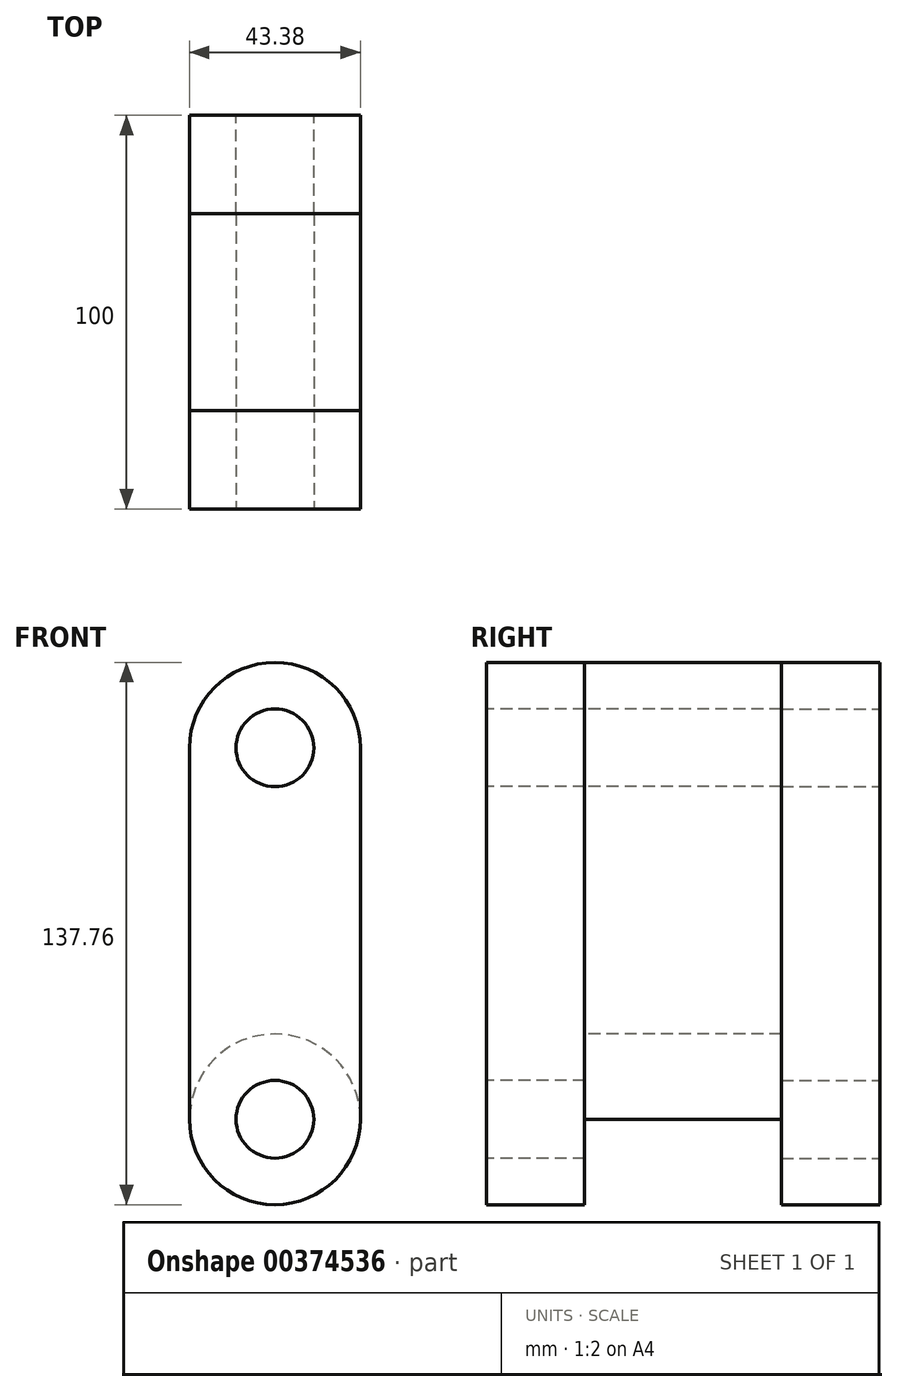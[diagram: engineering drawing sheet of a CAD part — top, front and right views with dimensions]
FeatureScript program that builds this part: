
annotation { "Feature Type Name" : "Feature", "Feature Type Description" : "" }
export const myFeature = defineFeature(function(context is Context, id is Id, definition is map)
    precondition{}
    {
        {
            var Q0;
            Q0=qCreatedBy(makeId("Front.planeOp"),FACE);
            var sketch = newSketch(context, id + "F0", { "sketchPlane" : qUnion([Q0])});
            skArc(sketch, "E0", {"start": v(-21.69, 0) * mm, "mid": v(0, -21.69) * mm, "end": v(21.69, 0) * mm});
            skArc(sketch, "E1", {"start": v(21.69, 94.38) * mm, "mid": v(0, 116.07) * mm, "end": v(-21.69, 94.38) * mm});
            skLineSegment(sketch, "E2", {"start": v(21.69, 94.38) * mm, "end": v(21.69, 0) * mm});
            skLineSegment(sketch, "E3", {"start": v(-21.69, 94.38) * mm, "end": v(-21.69, 0) * mm});
            skCircle(sketch, "E4", {"center": v(0, 94.38) * mm, "radius": 9.87 * mm});
            skCircle(sketch, "E5", {"center": v(0, 0) * mm, "radius": 9.87 * mm});
            skSolve(sketch);
        }
        {
            var Q0;
            Q0=makeQuery(id+"F0.imprint","IMPRINT",FACE,{"disambiguationData":[TD([[makeQuery(id+"F0.imprint","IMPRINT",EDGE,{"derivedFrom":sQuery(id+"F0.wireOp",EDGE,"E0")}),1.0]])]});
            extrude(context, id + "F1", {"entities" : qUnion([Q0]), "depth" : 25 * mm});
        }
        {
            var Q0;
            Q0=qCreatedBy(makeId("Front.planeOp"),FACE);
            cPlane(context, id + "F2", {"entities" : qUnion([Q0]), "cplaneType" : CPlaneType.OFFSET, "offset" : 50 * mm, "width" : 150 * mm, "height" : 150 * mm});
        }
        {
            var Q0;
            Q0=makeQuery(id+"F1.opExtrude","SWEPT_BODY",BODY,{"disambiguationData":[OSD([sQuery(id+"F0.wireOp",EDGE,"E0"),sQuery(id+"F0.wireOp",EDGE,"E1"),sQuery(id+"F0.wireOp",EDGE,"E2"),sQuery(id+"F0.wireOp",EDGE,"E3"),sQuery(id+"F0.wireOp",EDGE,"E4"),sQuery(id+"F0.wireOp",EDGE,"E5")])]});
            var Q1;
            Q1=qCreatedBy(id+"F2.planeOp",FACE);
            mirror(context, id + "F3", {"entities" : qUnion([Q0]), "mirrorPlane" : qUnion([Q1])});
        }
        {
            var Q0;
            Q0=makeQuery(id+"F3.opPattern","COPY",FACE,{"derivedFrom":makeQuery(id+"F1.opExtrude","CAP_FACE",FACE,{"disambiguationData":[OSD([sQuery(id+"F0.wireOp",EDGE,"E0"),sQuery(id+"F0.wireOp",EDGE,"E1"),sQuery(id+"F0.wireOp",EDGE,"E2"),sQuery(id+"F0.wireOp",EDGE,"E3"),sQuery(id+"F0.wireOp",EDGE,"E4"),sQuery(id+"F0.wireOp",EDGE,"E5")])],"isStart":false}),"instanceName":"1"});
            var sketch = newSketch(context, id + "F4", { "sketchPlane" : qUnion([Q0])});
            skCircle(sketch, "E6", {"center": v(0, 0) * mm, "radius": 21.69 * mm});
            skSolve(sketch);
        }
        {
            var Q0;
            {var subQ0=sQuery(id+"F4.wireOp",EDGE,"E6");Q0=makeQuery(id+"F4.imprint","IMPRINT",FACE,{"disambiguationData":[TD([[makeQuery(id+"F4.imprint","IMPRINT",EDGE,{"disambiguationData":[OD(0.0)],"derivedFrom":subQ0}),-1.0]])]});}
            extrude(context, id + "F5", {"entities" : qUnion([Q0]), "endBound" : BoundingType.UP_TO_NEXT, "depth" : 25 * mm});
        }
    });
